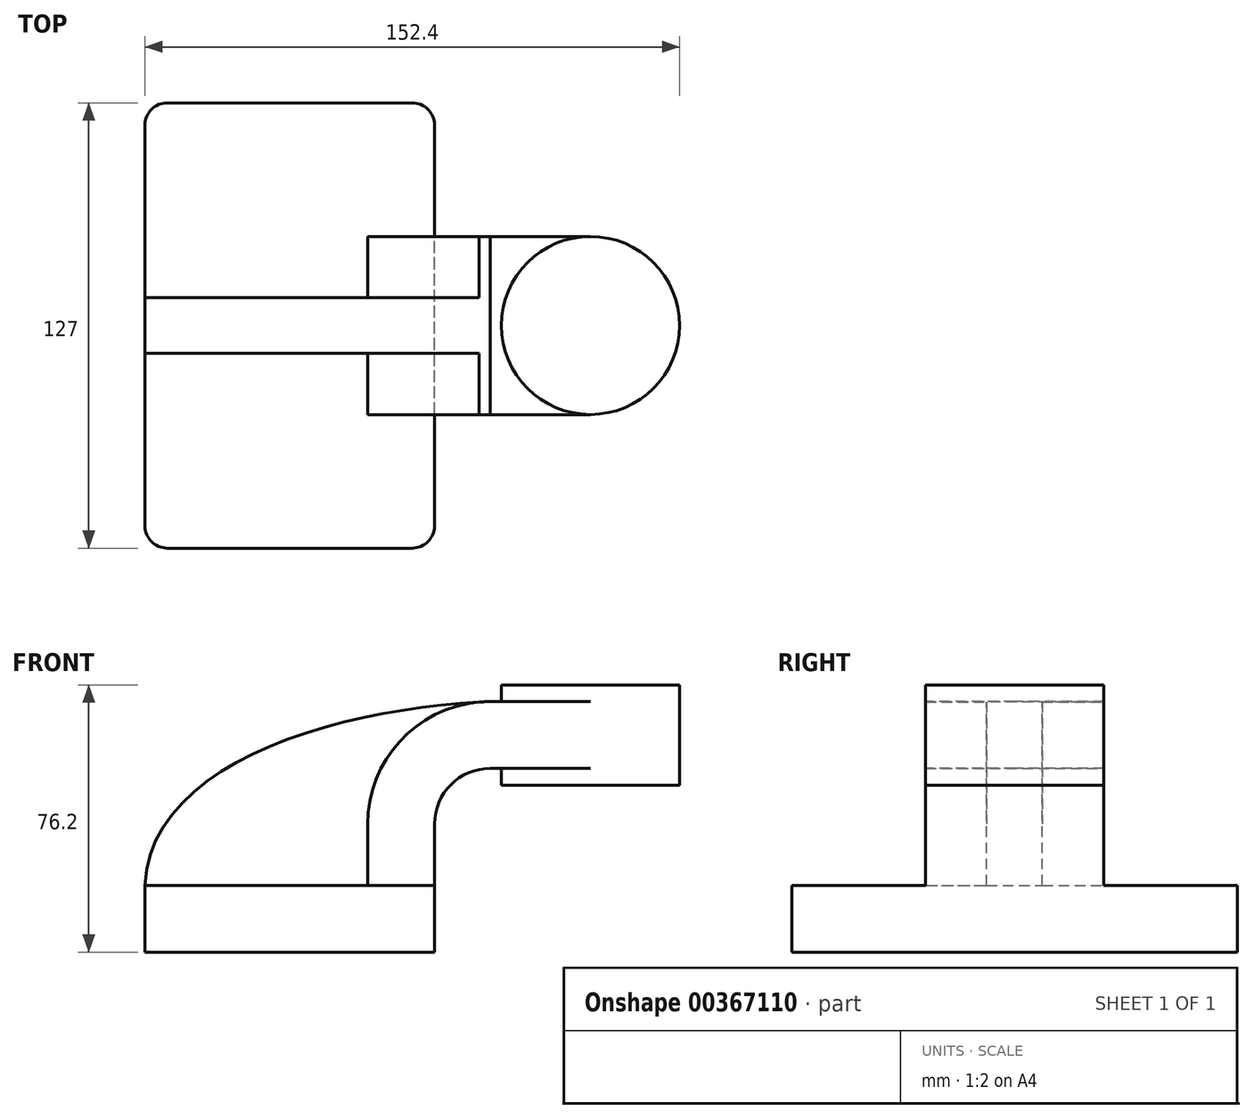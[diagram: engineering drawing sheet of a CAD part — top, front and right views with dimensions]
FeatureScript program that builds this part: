
annotation { "Feature Type Name" : "Feature", "Feature Type Description" : "" }
export const myFeature = defineFeature(function(context is Context, id is Id, definition is map)
    precondition{}
    {
        {
            var Q0;
            Q0=qCreatedBy(makeId("Front.planeOp"),FACE);
            var sketch = newSketch(context, id + "F0", { "sketchPlane" : qUnion([Q0])});
            skLineSegment(sketch, "E0.bottom", {"start": v(-76.52, -13.5) * mm, "end": v(6.03, -13.5) * mm});
            skLineSegment(sketch, "E0.top", {"start": v(-76.52, -32.56) * mm, "end": v(6.03, -32.56) * mm});
            skLineSegment(sketch, "E0.left", {"start": v(-76.52, -13.5) * mm, "end": v(-76.52, -32.56) * mm});
            skLineSegment(sketch, "E0.right", {"start": v(6.03, -13.5) * mm, "end": v(6.03, -32.56) * mm});
            skPoint(sketch, "E0.middle", {"position": v(-35.25, -23.03) * mm});
            skLineSegment(sketch, "E1.bottom", {"start": v(75.88, 15.07) * mm, "end": v(25.08, 15.07) * mm});
            skLineSegment(sketch, "E1.top", {"start": v(75.88, 43.64) * mm, "end": v(25.08, 43.64) * mm});
            skLineSegment(sketch, "E1.left", {"start": v(75.88, 15.07) * mm, "end": v(75.88, 43.64) * mm});
            skLineSegment(sketch, "E1.right", {"start": v(25.08, 15.07) * mm, "end": v(25.08, 43.64) * mm});
            skPoint(sketch, "E1.middle", {"position": v(50.48, 29.35) * mm});
            skLineSegment(sketch, "E2", {"start": v(6.03, -13.5) * mm, "end": v(6.03, 3.97) * mm});
            skArc(sketch, "E3", {"start": v(6.03, 3.97) * mm, "mid": v(10.68, 15.2) * mm, "end": v(21.9, 19.84) * mm});
            skLineSegment(sketch, "E4", {"start": v(21.9, 19.84) * mm, "end": v(50.48, 19.84) * mm});
            skLineSegment(sketch, "E5.0", {"start": v(21.9, 38.9) * mm, "end": v(50.48, 38.9) * mm});
            skArc(sketch, "E5.1", {"start": v(-13.02, 3.97) * mm, "mid": v(-2.8, 28.66) * mm, "end": v(21.9, 38.9) * mm});
            skLineSegment(sketch, "E5.2", {"start": v(-13.02, -13.5) * mm, "end": v(-13.02, 3.97) * mm});
            skLineSegment(sketch, "E6", {"start": v(50.48, 15.07) * mm, "end": v(50.48, 43.64) * mm});
            skFitSpline(sketch, "E7", {"points": [v(-76.52, -13.5) * mm, v(21.9, 38.9) * mm], "startDerivative": vector(4.7, 108.08) * mm, "endDerivative": vector(121.83, 4.58) * mm});
            skSolve(sketch);
        }
        {
            var Q0;
            Q0=makeQuery(id+"F0.imprint","IMPRINT",FACE,{"disambiguationData":[TD([[makeQuery(id+"F0.imprint","IMPRINT",EDGE,{"derivedFrom":sQuery(id+"F0.wireOp",EDGE,"E0.top")}),1.0]])]});
            extrude(context, id + "F1", {"entities" : qUnion([Q0]), "endBound" : BoundingType.SYMMETRIC, "depth" : 127 * mm});
        }
        {
            var Q0;
            {var subQ1=sQuery(id+"F0.wireOp",EDGE,"E2");Q0=makeQuery(id+"F0.imprint","IMPRINT",FACE,{"disambiguationData":[TD([[makeQuery(id+"F0.imprint","IMPRINT",EDGE,{"derivedFrom":subQ1}),1.0]])]});}
            var Q1;
            {var subQ0=sQuery(id+"F0.wireOp",EDGE,"E4");var subQ1=sQuery(id+"F0.wireOp",EDGE,"E1.right");var subQ2=makeQuery(id+"F0.imprint","INTERSECT",VERTEX,{"derivedFrom":[subQ1,subQ0]});Q1=makeQuery(id+"F0.imprint","IMPRINT",FACE,{"disambiguationData":[TD([[makeQuery(id+"F0.imprint","IMPRINT",EDGE,{"disambiguationData":[TD([[subQ2,-1.0]])],"derivedFrom":subQ1}),-1.0]])]});}
            extrude(context, id + "F2", {"entities" : qUnion([Q0, Q1]), "operationType" : NewBodyOperationType.ADD, "endBound" : BoundingType.SYMMETRIC, "depth" : 50.8 * mm});
        }
        {
            var Q0;
            {var subQ0=sQuery(id+"F0.wireOp",EDGE,"E1.left");Q0=makeQuery(id+"F0.imprint","IMPRINT",FACE,{"disambiguationData":[TD([[makeQuery(id+"F0.imprint","IMPRINT",EDGE,{"derivedFrom":subQ0}),1.0]])]});}
            var Q1;
            Q1=sQuery(id+"F0.wireOp",EDGE,"E6");
            revolve(context, id + "F3", {"operationType" : NewBodyOperationType.ADD, "entities" : qUnion([Q0]), "axis" : qUnion([Q1]), "revolveType" : RevolveType.FULL});
        }
        {
            var Q0;
            {var subQ3=sQuery(id+"F0.wireOp",EDGE,"E5.2");Q0=makeQuery(id+"F0.imprint","IMPRINT",FACE,{"disambiguationData":[TD([[makeQuery(id+"F0.imprint","IMPRINT",EDGE,{"derivedFrom":subQ3}),1.0]])]});}
            extrude(context, id + "F4", {"entities" : qUnion([Q0]), "operationType" : NewBodyOperationType.ADD, "endBound" : BoundingType.SYMMETRIC, "depth" : 15.88 * mm});
        }
        {
            var Q0;
            Q0=makeQuery(id+"F1.opExtrude","CAP_EDGE",EDGE,{"disambiguationData":[OSD([sQuery(id+"F0.wireOp",EDGE,"E0.right")])],"isStart":false});
            var Q1;
            Q1=makeQuery(id+"F1.opExtrude","CAP_EDGE",EDGE,{"disambiguationData":[OSD([sQuery(id+"F0.wireOp",EDGE,"E0.left")])],"isStart":false});
            var Q2;
            Q2=makeQuery(id+"F1.opExtrude","CAP_EDGE",EDGE,{"disambiguationData":[OSD([sQuery(id+"F0.wireOp",EDGE,"E0.right")])],"isStart":true});
            var Q3;
            Q3=makeQuery(id+"F1.opExtrude","CAP_EDGE",EDGE,{"disambiguationData":[OSD([sQuery(id+"F0.wireOp",EDGE,"E0.left")])],"isStart":true});
            fillet(context, id + "F5", {"entities" : qUnion([Q0, Q1, Q2, Q3]), "radius" : 6.35 * mm, "tangentPropagation" : true, "allowEdgeOverflow" : false});
        }
    });
